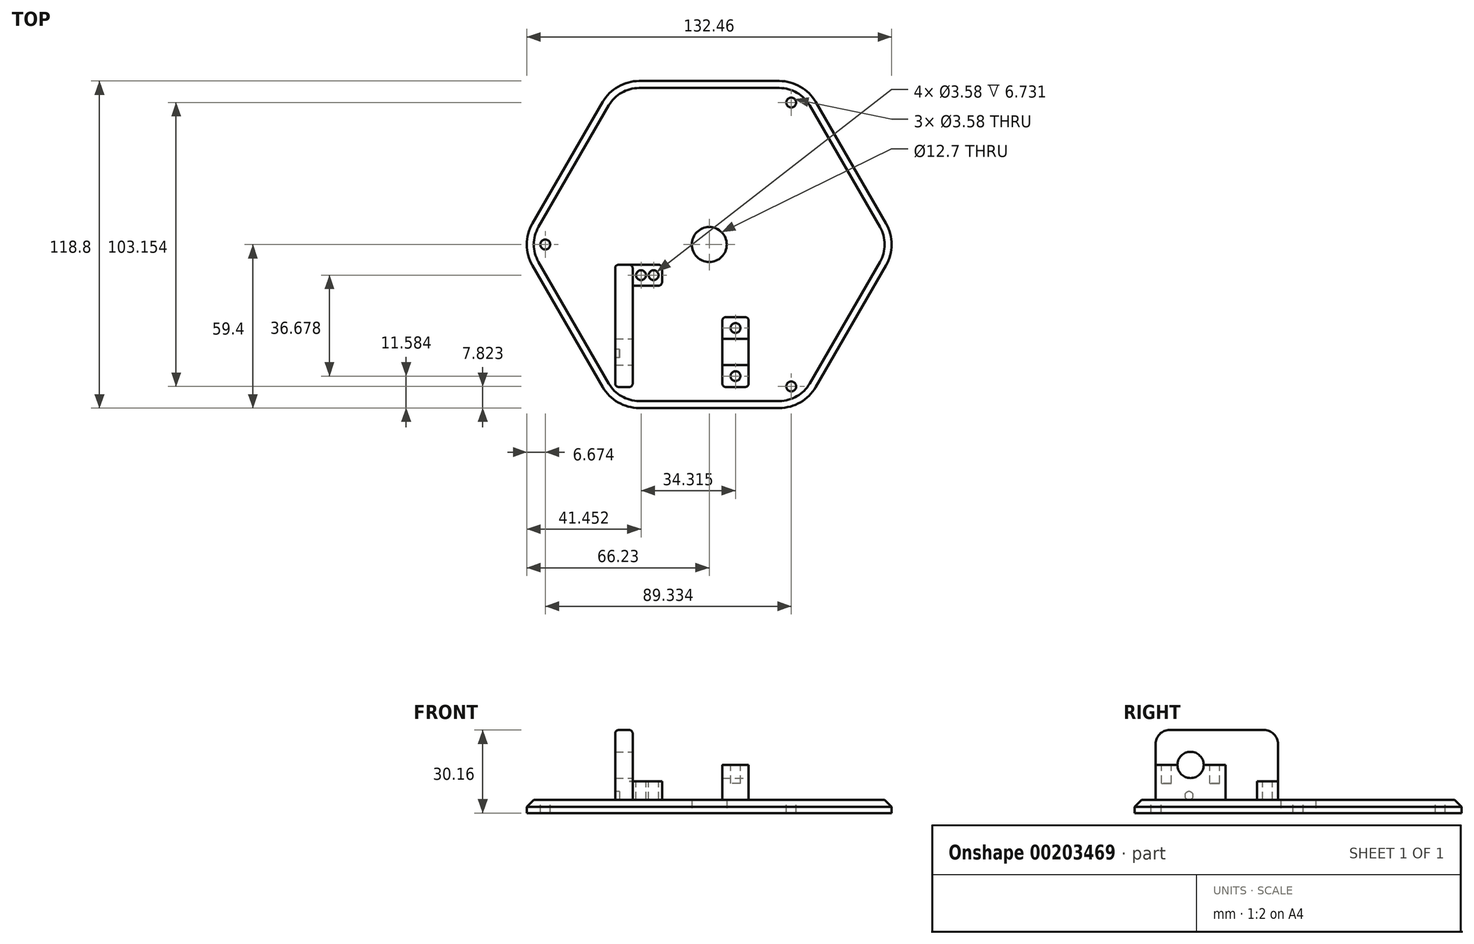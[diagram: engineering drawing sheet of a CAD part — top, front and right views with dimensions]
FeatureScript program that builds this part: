
annotation { "Feature Type Name" : "Feature", "Feature Type Description" : "" }
export const myFeature = defineFeature(function(context is Context, id is Id, definition is map)
    precondition{}
    {
        {
            var Q0;
            Q0=qCreatedBy(makeId("Top.planeOp"),FACE);
            var sketch = newSketch(context, id + "F0", { "sketchPlane" : qUnion([Q0])});
            skCircle(sketch, "E0.cCircle", {"center": v(0, 0) * mm, "radius": 59.4 * mm, "construction": true});
            skLineSegment(sketch, "E0.0", {"start": v(34.3, -59.4) * mm, "end": v(-34.3, -59.4) * mm});
            skLineSegment(sketch, "E0.1", {"start": v(-34.3, -59.4) * mm, "end": v(-68.59, 0) * mm});
            skLineSegment(sketch, "E0.2", {"start": v(-68.59, 0) * mm, "end": v(-34.3, 59.4) * mm});
            skLineSegment(sketch, "E0.3", {"start": v(-34.3, 59.4) * mm, "end": v(34.3, 59.4) * mm});
            skLineSegment(sketch, "E0.4", {"start": v(34.3, 59.4) * mm, "end": v(68.59, 0) * mm});
            skLineSegment(sketch, "E0.5", {"start": v(68.59, 0) * mm, "end": v(34.3, -59.4) * mm});
            skPoint(sketch, "E0.0.midPoint", {"position": v(0, -59.4) * mm});
            skCircle(sketch, "E1", {"center": v(0, 0) * mm, "radius": 6.35 * mm});
            skSolve(sketch);
        }
        {
            var Q0;
            Q0=makeQuery(id+"F0.imprint","IMPRINT",FACE,{"disambiguationData":[TD([[makeQuery(id+"F0.imprint","IMPRINT",EDGE,{"derivedFrom":sQuery(id+"F0.wireOp",EDGE,"E0.0")}),-1.0]])]});
            extrude(context, id + "F1", {"entities" : qUnion([Q0]), "depth" : 4.76 * mm});
        }
        {
            var Q0;
            Q0=makeQuery(id+"F1.opExtrude","CAP_FACE",FACE,{"disambiguationData":[OSD([sQuery(id+"F0.wireOp",EDGE,"E0.0"),sQuery(id+"F0.wireOp",EDGE,"E0.1"),sQuery(id+"F0.wireOp",EDGE,"E0.2"),sQuery(id+"F0.wireOp",EDGE,"E0.3"),sQuery(id+"F0.wireOp",EDGE,"E0.4"),sQuery(id+"F0.wireOp",EDGE,"E0.5"),sQuery(id+"F0.wireOp",EDGE,"E1")])],"isStart":false});
            var sketch = newSketch(context, id + "F2", { "sketchPlane" : qUnion([Q0])});
            skLineSegment(sketch, "E2.bottom", {"start": v(-34.16, -51.78) * mm, "end": v(-27.81, -51.78) * mm});
            skLineSegment(sketch, "E2.top", {"start": v(-34.16, -7.33) * mm, "end": v(-27.81, -7.33) * mm});
            skLineSegment(sketch, "E2.left", {"start": v(-34.16, -51.78) * mm, "end": v(-34.16, -7.33) * mm});
            skLineSegment(sketch, "E2.right", {"start": v(-27.81, -51.78) * mm, "end": v(-27.81, -7.33) * mm});
            skLineSegment(sketch, "E3.bottom", {"start": v(-27.81, -7.33) * mm, "end": v(-17.15, -7.33) * mm});
            skLineSegment(sketch, "E3.top", {"start": v(-27.81, -14.95) * mm, "end": v(-17.15, -14.95) * mm});
            skLineSegment(sketch, "E3.left", {"start": v(-27.81, -7.33) * mm, "end": v(-27.81, -14.95) * mm});
            skLineSegment(sketch, "E3.right", {"start": v(-17.15, -7.33) * mm, "end": v(-17.15, -14.95) * mm});
            skLineSegment(sketch, "E4.bottom", {"start": v(4.78, -51.78) * mm, "end": v(14.3, -51.78) * mm});
            skLineSegment(sketch, "E4.top", {"start": v(4.78, -26.38) * mm, "end": v(14.3, -26.38) * mm});
            skLineSegment(sketch, "E4.left", {"start": v(4.78, -51.78) * mm, "end": v(4.78, -26.38) * mm});
            skLineSegment(sketch, "E4.right", {"start": v(14.3, -51.78) * mm, "end": v(14.3, -26.38) * mm});
            skLineSegment(sketch, "E5.1.0", {"start": v(37.7, 38.27) * mm, "end": v(15.7, 25.57) * mm});
            skLineSegment(sketch, "E5.1.1", {"start": v(42.45, 30.02) * mm, "end": v(20.46, 17.32) * mm});
            skLineSegment(sketch, "E5.1.2", {"start": v(20.46, 17.32) * mm, "end": v(15.7, 25.57) * mm});
            skLineSegment(sketch, "E5.1.3", {"start": v(61.92, -3.7) * mm, "end": v(23.43, -25.92) * mm});
            skLineSegment(sketch, "E5.1.4", {"start": v(58.75, 1.8) * mm, "end": v(20.25, -20.42) * mm});
            skLineSegment(sketch, "E5.1.5", {"start": v(20.25, -20.42) * mm, "end": v(14.92, -11.18) * mm});
            skLineSegment(sketch, "E5.1.6", {"start": v(26.85, -16.61) * mm, "end": v(21.52, -7.37) * mm});
            skLineSegment(sketch, "E5.1.7", {"start": v(42.45, 30.02) * mm, "end": v(37.7, 38.27) * mm});
            skLineSegment(sketch, "E5.1.8", {"start": v(14.92, -11.18) * mm, "end": v(21.52, -7.37) * mm});
            skLineSegment(sketch, "E5.1.9", {"start": v(61.92, -3.7) * mm, "end": v(58.75, 1.8) * mm});
            skLineSegment(sketch, "E5.1.10", {"start": v(23.43, -25.92) * mm, "end": v(20.25, -20.42) * mm});
            skLineSegment(sketch, "E5.1.11", {"start": v(20.25, -20.42) * mm, "end": v(26.85, -16.61) * mm});
            skLineSegment(sketch, "E5.2.0", {"start": v(-52, 13.5) * mm, "end": v(-30, 0.8) * mm});
            skLineSegment(sketch, "E5.2.1", {"start": v(-47.23, 21.75) * mm, "end": v(-25.23, 9.05) * mm});
            skLineSegment(sketch, "E5.2.2", {"start": v(-25.23, 9.05) * mm, "end": v(-30, 0.8) * mm});
            skLineSegment(sketch, "E5.2.3", {"start": v(-27.76, 55.47) * mm, "end": v(10.74, 33.25) * mm});
            skLineSegment(sketch, "E5.2.4", {"start": v(-30.93, 49.98) * mm, "end": v(7.56, 27.75) * mm});
            skLineSegment(sketch, "E5.2.5", {"start": v(7.56, 27.75) * mm, "end": v(2.23, 18.51) * mm});
            skLineSegment(sketch, "E5.2.6", {"start": v(0.96, 31.56) * mm, "end": v(-4.37, 22.32) * mm});
            skLineSegment(sketch, "E5.2.7", {"start": v(-47.23, 21.75) * mm, "end": v(-52, 13.5) * mm});
            skLineSegment(sketch, "E5.2.8", {"start": v(2.23, 18.51) * mm, "end": v(-4.37, 22.32) * mm});
            skLineSegment(sketch, "E5.2.9", {"start": v(-27.76, 55.47) * mm, "end": v(-30.93, 49.98) * mm});
            skLineSegment(sketch, "E5.2.10", {"start": v(10.74, 33.25) * mm, "end": v(7.56, 27.75) * mm});
            skLineSegment(sketch, "E5.2.11", {"start": v(7.56, 27.75) * mm, "end": v(0.96, 31.56) * mm});
            skPoint(sketch, "E5.center", {"position": v(0, 0) * mm});
            skSolve(sketch);
        }
        {
            var Q0;
            Q0=makeQuery(id+"F2.imprint","IMPRINT",FACE,{"disambiguationData":[TD([[makeQuery(id+"F2.imprint","IMPRINT",EDGE,{"derivedFrom":sQuery(id+"F2.wireOp",EDGE,"E2.bottom")}),1.0]])]});
            extrude(context, id + "F3", {"entities" : qUnion([Q0]), "operationType" : NewBodyOperationType.ADD, "depth" : 25.4 * mm});
        }
        {
            var Q0;
            Q0=makeQuery(id+"F2.imprint","IMPRINT",FACE,{"disambiguationData":[TD([[makeQuery(id+"F2.imprint","IMPRINT",EDGE,{"derivedFrom":sQuery(id+"F2.wireOp",EDGE,"E3.bottom")}),-1.0]])]});
            extrude(context, id + "F4", {"entities" : qUnion([Q0]), "operationType" : NewBodyOperationType.ADD, "depth" : 6.73 * mm});
        }
        {
            var Q0;
            Q0=makeQuery(id+"F2.imprint","IMPRINT",FACE,{"disambiguationData":[TD([[makeQuery(id+"F2.imprint","IMPRINT",EDGE,{"derivedFrom":sQuery(id+"F2.wireOp",EDGE,"E4.bottom")}),1.0]])]});
            extrude(context, id + "F5", {"entities" : qUnion([Q0]), "operationType" : NewBodyOperationType.ADD, "depth" : 12.7 * mm});
        }
        {
            var Q0;
            Q0=makeQuery(id+"F5.opExtrude","SWEPT_FACE",FACE,{"disambiguationData":[OSD([sQuery(id+"F2.wireOp",EDGE,"E4.right")])]});
            var sketch = newSketch(context, id + "F6", { "sketchPlane" : qUnion([Q0])});
            skCircle(sketch, "E6", {"center": v(-39.08, 17.46) * mm, "radius": 4.78 * mm});
            skSolve(sketch);
        }
        {
            var Q0;
            {var subQ0=sQuery(id+"F6.wireOp",EDGE,"E6");var subQ1=makeQuery(id+"F5.opExtrude","CAP_EDGE",EDGE,{"disambiguationData":[OSD([sQuery(id+"F2.wireOp",EDGE,"E4.right")])],"isStart":false});var subQ2=makeQuery(id+"F6.imprint","INTERSECT",VERTEX,{"disambiguationData":[OD(0.0)],"derivedFrom":[subQ1,subQ0]});Q0=makeQuery(id+"F6.imprint","IMPRINT",FACE,{"disambiguationData":[TD([[makeQuery(id+"F6.imprint","IMPRINT",EDGE,{"disambiguationData":[TD([[subQ2,-1.0]])],"derivedFrom":subQ0}),1.0]])]});}
            var Q1;
            {var subQ0=sQuery(id+"F6.wireOp",EDGE,"E6");var subQ1=makeQuery(id+"F5.opExtrude","CAP_EDGE",EDGE,{"disambiguationData":[OSD([sQuery(id+"F2.wireOp",EDGE,"E4.right")])],"isStart":false});var subQ2=makeQuery(id+"F6.imprint","INTERSECT",VERTEX,{"disambiguationData":[OD(0.0)],"derivedFrom":[subQ1,subQ0]});Q1=makeQuery(id+"F6.imprint","IMPRINT",FACE,{"disambiguationData":[TD([[makeQuery(id+"F6.imprint","IMPRINT",EDGE,{"disambiguationData":[TD([[subQ2,1.0]])],"derivedFrom":subQ0}),1.0]])]});}
            extrude(context, id + "F7", {"entities" : qUnion([Q0, Q1]), "operationType" : NewBodyOperationType.REMOVE, "oppositeDirection" : true, "depth" : 52.07 * mm});
        }
        {
            var Q0;
            {var subQ0=sQuery(id+"F2.wireOp",EDGE,"E4.top");var subQ1=sQuery(id+"F2.wireOp",EDGE,"E4.left");var subQ2=sQuery(id+"F2.wireOp",EDGE,"E4.right");Q0=makeQuery(id+"F7.boolean.opBoolean","SPLIT",FACE,{"disambiguationData":[TD([makeQuery(id+"F5.opExtrude","SWEPT_FACE",FACE,{"disambiguationData":[OSD([subQ0])]})])],"derivedFrom":makeQuery(id+"F5.opExtrude","CAP_FACE",FACE,{"disambiguationData":[OSD([sQuery(id+"F2.wireOp",EDGE,"E4.bottom"),subQ0,subQ1,subQ2])],"isStart":false})});}
            var sketch = newSketch(context, id + "F8", { "sketchPlane" : qUnion([Q0])});
            skPoint(sketch, "E7", {"position": v(9.54, -30.34) * mm});
            skPoint(sketch, "E7.positionSnap0", {"position": v(9.54, -26.38) * mm});
            skPoint(sketch, "E7.positionSnap1", {"position": v(4.78, -30.34) * mm});
            skCircle(sketch, "E8", {"center": v(9.54, -30.34) * mm, "radius": 1.8 * mm});
            skSolve(sketch);
        }
        {
            var Q0;
            {var subQ0=sQuery(id+"F2.wireOp",EDGE,"E4.bottom");var subQ1=sQuery(id+"F2.wireOp",EDGE,"E4.left");var subQ2=sQuery(id+"F2.wireOp",EDGE,"E4.right");Q0=makeQuery(id+"F7.boolean.opBoolean","SPLIT",FACE,{"disambiguationData":[TD([makeQuery(id+"F5.opExtrude","SWEPT_FACE",FACE,{"disambiguationData":[OSD([subQ0])]})])],"derivedFrom":makeQuery(id+"F5.opExtrude","CAP_FACE",FACE,{"disambiguationData":[OSD([subQ0,sQuery(id+"F2.wireOp",EDGE,"E4.top"),subQ1,subQ2])],"isStart":false})});}
            var sketch = newSketch(context, id + "F9", { "sketchPlane" : qUnion([Q0])});
            skPoint(sketch, "E9", {"position": v(9.54, -47.82) * mm});
            skPoint(sketch, "E9.positionSnap0", {"position": v(9.54, -51.78) * mm});
            skPoint(sketch, "E9.positionSnap1", {"position": v(4.78, -47.82) * mm});
            skCircle(sketch, "E10", {"center": v(9.54, -47.82) * mm, "radius": 1.8 * mm});
            skSolve(sketch);
        }
        {
            var Q0;
            Q0=makeQuery(id+"F8.imprint","IMPRINT",FACE,{"disambiguationData":[TD([[makeQuery(id+"F8.imprint","IMPRINT",EDGE,{"derivedFrom":sQuery(id+"F8.wireOp",EDGE,"E8")}),1.0]])]});
            var Q1;
            Q1=makeQuery(id+"F9.imprint","IMPRINT",FACE,{"disambiguationData":[TD([[makeQuery(id+"F9.imprint","IMPRINT",EDGE,{"derivedFrom":sQuery(id+"F9.wireOp",EDGE,"E10")}),1.0]])]});
            extrude(context, id + "F10", {"entities" : qUnion([Q0, Q1]), "operationType" : NewBodyOperationType.REMOVE, "oppositeDirection" : true, "depth" : 6.73 * mm});
        }
        {
            var Q0;
            Q0=makeQuery(id+"F4.opExtrude","CAP_FACE",FACE,{"disambiguationData":[OSD([sQuery(id+"F2.wireOp",EDGE,"E3.bottom"),sQuery(id+"F2.wireOp",EDGE,"E3.top"),sQuery(id+"F2.wireOp",EDGE,"E3.left"),sQuery(id+"F2.wireOp",EDGE,"E3.right")])],"isStart":false});
            var sketch = newSketch(context, id + "F11", { "sketchPlane" : qUnion([Q0])});
            skCircle(sketch, "E11", {"center": v(-24.78, -11.14) * mm, "radius": 1.8 * mm});
            skPoint(sketch, "E11.centerSnap0", {"position": v(-27.81, -11.14) * mm});
            skCircle(sketch, "E12", {"center": v(-20.2, -11.14) * mm, "radius": 1.8 * mm});
            skSolve(sketch);
        }
        {
            var Q0;
            Q0=makeQuery(id+"F11.imprint","IMPRINT",FACE,{"disambiguationData":[TD([[makeQuery(id+"F11.imprint","IMPRINT",EDGE,{"derivedFrom":sQuery(id+"F11.wireOp",EDGE,"E11")}),1.0]])]});
            var Q1;
            Q1=makeQuery(id+"F11.imprint","IMPRINT",FACE,{"disambiguationData":[TD([[makeQuery(id+"F11.imprint","IMPRINT",EDGE,{"derivedFrom":sQuery(id+"F11.wireOp",EDGE,"E12")}),1.0]])]});
            extrude(context, id + "F12", {"entities" : qUnion([Q0, Q1]), "operationType" : NewBodyOperationType.REMOVE, "oppositeDirection" : true, "depth" : 6.73 * mm});
        }
        {
            var Q0;
            Q0=makeQuery(id+"F3.opExtrude","CAP_EDGE",EDGE,{"disambiguationData":[OSD([sQuery(id+"F2.wireOp",EDGE,"E2.top")])],"isStart":false});
            var Q1;
            Q1=makeQuery(id+"F3.opExtrude","CAP_EDGE",EDGE,{"disambiguationData":[OSD([sQuery(id+"F2.wireOp",EDGE,"E2.bottom")])],"isStart":false});
            fillet(context, id + "F13", {"entities" : qUnion([Q0, Q1]), "radius" : 5.08 * mm, "tangentPropagation" : true, "allowEdgeOverflow" : false});
        }
        {
            var Q0;
            Q0=makeQuery(id+"F3.opExtrude","CAP_EDGE",EDGE,{"disambiguationData":[OSD([sQuery(id+"F2.wireOp",EDGE,"E2.left")])],"isStart":true});
            var Q1;
            Q1=makeQuery(id+"F3.opExtrude","CAP_EDGE",EDGE,{"disambiguationData":[OSD([sQuery(id+"F2.wireOp",EDGE,"E2.bottom")])],"isStart":true});
            var Q2;
            Q2=makeQuery(id+"F3.opExtrude","SWEPT_EDGE",EDGE,{"disambiguationData":[OSD([sQuery(id+"F2.wireOp",EDGE,"E2.bottom"),sQuery(id+"F2.wireOp",EDGE,"E2.left")])]});
            var Q3;
            Q3=makeQuery(id+"F3.opExtrude","SWEPT_EDGE",EDGE,{"disambiguationData":[OSD([sQuery(id+"F2.wireOp",EDGE,"E2.bottom"),sQuery(id+"F2.wireOp",EDGE,"E2.right")])]});
            var Q4;
            Q4=makeQuery(id+"F4.opExtrude","CAP_EDGE",EDGE,{"disambiguationData":[OSD([sQuery(id+"F2.wireOp",EDGE,"E3.top")])],"isStart":true});
            var Q5;
            Q5=makeQuery(id+"F4.opExtrude","CAP_EDGE",EDGE,{"disambiguationData":[OSD([sQuery(id+"F2.wireOp",EDGE,"E3.right")])],"isStart":true});
            var Q6;
            Q6=makeQuery(id+"F4.opExtrude","SWEPT_EDGE",EDGE,{"disambiguationData":[OSD([sQuery(id+"F2.wireOp",EDGE,"E3.bottom"),sQuery(id+"F2.wireOp",EDGE,"E3.right")])]});
            var Q7;
            Q7=makeQuery(id+"F4.opExtrude","SWEPT_EDGE",EDGE,{"disambiguationData":[OSD([sQuery(id+"F2.wireOp",EDGE,"E3.top"),sQuery(id+"F2.wireOp",EDGE,"E3.right")])]});
            var Q8;
            Q8=makeQuery(id+"F5.opExtrude","SWEPT_EDGE",EDGE,{"disambiguationData":[OSD([sQuery(id+"F2.wireOp",EDGE,"E4.bottom"),sQuery(id+"F2.wireOp",EDGE,"E4.left")])]});
            var Q9;
            Q9=makeQuery(id+"F5.opExtrude","SWEPT_EDGE",EDGE,{"disambiguationData":[OSD([sQuery(id+"F2.wireOp",EDGE,"E4.bottom"),sQuery(id+"F2.wireOp",EDGE,"E4.right")])]});
            var Q10;
            Q10=makeQuery(id+"F5.opExtrude","SWEPT_EDGE",EDGE,{"disambiguationData":[OSD([sQuery(id+"F2.wireOp",EDGE,"E4.top"),sQuery(id+"F2.wireOp",EDGE,"E4.right")])]});
            var Q11;
            Q11=makeQuery(id+"F5.opExtrude","SWEPT_EDGE",EDGE,{"disambiguationData":[OSD([sQuery(id+"F2.wireOp",EDGE,"E4.top"),sQuery(id+"F2.wireOp",EDGE,"E4.left")])]});
            fillet(context, id + "F14", {"entities" : qUnion([Q0, Q1, Q2, Q3, Q4, Q5, Q6, Q7, Q8, Q9, Q10, Q11]), "radius" : 1.27 * mm, "tangentPropagation" : true, "allowEdgeOverflow" : false});
        }
        {
            var Q0;
            Q0=makeQuery(id+"F3.opExtrude","SWEPT_FACE",FACE,{"disambiguationData":[OSD([sQuery(id+"F2.wireOp",EDGE,"E2.left")])]});
            var sketch = newSketch(context, id + "F15", { "sketchPlane" : qUnion([Q0])});
            skCircle(sketch, "E13", {"center": v(39.64, 6.29) * mm, "radius": 1.52 * mm});
            skSolve(sketch);
        }
        {
            var Q0;
            {var subQ0=sQuery(id+"F15.wireOp",EDGE,"E13");var subQ1=sQuery(id+"F2.wireOp",EDGE,"E2.left");var subQ2=makeQuery(id+"F14.opFillet","BLEND_EDGE",EDGE,{"blendedFrom":[makeQuery(id+"F3.opExtrude","CAP_EDGE",EDGE,{"disambiguationData":[OSD([subQ1])],"isStart":true}),makeQuery(id+"F3.opExtrude","SWEPT_FACE",FACE,{"disambiguationData":[OSD([subQ1])]})],"blendedInto":[makeQuery(id+"F3.opExtrude","SWEPT_FACE",FACE,{"disambiguationData":[OSD([subQ1])]})]});var subQ3=makeQuery(id+"F15.imprint","INTERSECT",VERTEX,{"disambiguationData":[OD(0.0)],"derivedFrom":[subQ2,subQ0]});Q0=makeQuery(id+"F15.imprint","IMPRINT",FACE,{"disambiguationData":[TD([[makeQuery(id+"F15.imprint","IMPRINT",EDGE,{"disambiguationData":[TD([[subQ3,1.0]])],"derivedFrom":subQ0}),1.0]])]});}
            var Q1;
            {var subQ0=sQuery(id+"F15.wireOp",EDGE,"E13");var subQ1=sQuery(id+"F2.wireOp",EDGE,"E2.left");var subQ2=makeQuery(id+"F14.opFillet","BLEND_EDGE",EDGE,{"blendedFrom":[makeQuery(id+"F3.opExtrude","CAP_EDGE",EDGE,{"disambiguationData":[OSD([subQ1])],"isStart":true}),makeQuery(id+"F3.opExtrude","SWEPT_FACE",FACE,{"disambiguationData":[OSD([subQ1])]})],"blendedInto":[makeQuery(id+"F3.opExtrude","SWEPT_FACE",FACE,{"disambiguationData":[OSD([subQ1])]})]});var subQ3=makeQuery(id+"F15.imprint","INTERSECT",VERTEX,{"disambiguationData":[OD(0.0)],"derivedFrom":[subQ2,subQ0]});Q1=makeQuery(id+"F15.imprint","IMPRINT",FACE,{"disambiguationData":[TD([[makeQuery(id+"F15.imprint","IMPRINT",EDGE,{"disambiguationData":[TD([[subQ3,-1.0]])],"derivedFrom":subQ0}),1.0]])]});}
            extrude(context, id + "F16", {"entities" : qUnion([Q0, Q1]), "operationType" : NewBodyOperationType.REMOVE, "endBound" : BoundingType.SYMMETRIC, "oppositeDirection" : true, "depth" : 3.17 * mm});
        }
        {
            var Q0;
            Q0=makeQuery(id+"F1.opExtrude","SWEPT_EDGE",EDGE,{"disambiguationData":[OSD([sQuery(id+"F0.wireOp",EDGE,"E0.2"),sQuery(id+"F0.wireOp",EDGE,"E0.3")])]});
            var Q1;
            Q1=makeQuery(id+"F1.opExtrude","SWEPT_EDGE",EDGE,{"disambiguationData":[OSD([sQuery(id+"F0.wireOp",EDGE,"E0.1"),sQuery(id+"F0.wireOp",EDGE,"E0.2")])]});
            var Q2;
            Q2=makeQuery(id+"F1.opExtrude","SWEPT_EDGE",EDGE,{"disambiguationData":[OSD([sQuery(id+"F0.wireOp",EDGE,"E0.3"),sQuery(id+"F0.wireOp",EDGE,"E0.4")])]});
            var Q3;
            Q3=makeQuery(id+"F1.opExtrude","SWEPT_EDGE",EDGE,{"disambiguationData":[OSD([sQuery(id+"F0.wireOp",EDGE,"E0.0"),sQuery(id+"F0.wireOp",EDGE,"E0.1")])]});
            var Q4;
            Q4=makeQuery(id+"F1.opExtrude","SWEPT_EDGE",EDGE,{"disambiguationData":[OSD([sQuery(id+"F0.wireOp",EDGE,"E0.0"),sQuery(id+"F0.wireOp",EDGE,"E0.5")])]});
            var Q5;
            Q5=makeQuery(id+"F1.opExtrude","SWEPT_EDGE",EDGE,{"disambiguationData":[OSD([sQuery(id+"F0.wireOp",EDGE,"E0.4"),sQuery(id+"F0.wireOp",EDGE,"E0.5")])]});
            fillet(context, id + "F17", {"entities" : qUnion([Q0, Q1, Q2, Q3, Q4, Q5]), "radius" : 15.24 * mm, "tangentPropagation" : true, "allowEdgeOverflow" : false});
        }
        {
            var Q0;
            Q0=makeQuery(id+"F1.opExtrude","CAP_EDGE",EDGE,{"disambiguationData":[OSD([sQuery(id+"F0.wireOp",EDGE,"E0.2")])],"isStart":false});
            var Q1;
            Q1=makeQuery(id+"F1.opExtrude","CAP_EDGE",EDGE,{"disambiguationData":[OSD([sQuery(id+"F0.wireOp",EDGE,"E0.1")])],"isStart":false});
            var Q2;
            {var subQ0=sQuery(id+"F0.wireOp",EDGE,"E0.2");var subQ1=sQuery(id+"F0.wireOp",EDGE,"E0.1");Q2=makeQuery(id+"F17.opFillet","BLEND_EDGE",EDGE,{"blendedFrom":[makeQuery(id+"F1.opExtrude","SWEPT_EDGE",EDGE,{"disambiguationData":[OSD([subQ1,subQ0])]}),makeQuery(id+"F1.opExtrude","CAP_FACE",FACE,{"disambiguationData":[OSD([sQuery(id+"F0.wireOp",EDGE,"E0.0"),subQ1,subQ0,sQuery(id+"F0.wireOp",EDGE,"E0.3"),sQuery(id+"F0.wireOp",EDGE,"E0.4"),sQuery(id+"F0.wireOp",EDGE,"E0.5"),sQuery(id+"F0.wireOp",EDGE,"E1")])],"isStart":false})],"blendedInto":[makeQuery(id+"F1.opExtrude","CAP_FACE",FACE,{"disambiguationData":[OSD([sQuery(id+"F0.wireOp",EDGE,"E0.0"),subQ1,subQ0,sQuery(id+"F0.wireOp",EDGE,"E0.3"),sQuery(id+"F0.wireOp",EDGE,"E0.4"),sQuery(id+"F0.wireOp",EDGE,"E0.5"),sQuery(id+"F0.wireOp",EDGE,"E1")])],"isStart":false})]});}
            var Q3;
            {var subQ0=sQuery(id+"F0.wireOp",EDGE,"E0.1");var subQ1=sQuery(id+"F0.wireOp",EDGE,"E0.0");Q3=makeQuery(id+"F17.opFillet","BLEND_EDGE",EDGE,{"blendedFrom":[makeQuery(id+"F1.opExtrude","SWEPT_EDGE",EDGE,{"disambiguationData":[OSD([subQ1,subQ0])]}),makeQuery(id+"F1.opExtrude","CAP_FACE",FACE,{"disambiguationData":[OSD([subQ1,subQ0,sQuery(id+"F0.wireOp",EDGE,"E0.2"),sQuery(id+"F0.wireOp",EDGE,"E0.3"),sQuery(id+"F0.wireOp",EDGE,"E0.4"),sQuery(id+"F0.wireOp",EDGE,"E0.5"),sQuery(id+"F0.wireOp",EDGE,"E1")])],"isStart":false})],"blendedInto":[makeQuery(id+"F1.opExtrude","CAP_FACE",FACE,{"disambiguationData":[OSD([subQ1,subQ0,sQuery(id+"F0.wireOp",EDGE,"E0.2"),sQuery(id+"F0.wireOp",EDGE,"E0.3"),sQuery(id+"F0.wireOp",EDGE,"E0.4"),sQuery(id+"F0.wireOp",EDGE,"E0.5"),sQuery(id+"F0.wireOp",EDGE,"E1")])],"isStart":false})]});}
            var Q4;
            Q4=makeQuery(id+"F1.opExtrude","CAP_EDGE",EDGE,{"disambiguationData":[OSD([sQuery(id+"F0.wireOp",EDGE,"E0.0")])],"isStart":false});
            var Q5;
            {var subQ0=sQuery(id+"F0.wireOp",EDGE,"E0.5");var subQ1=sQuery(id+"F0.wireOp",EDGE,"E0.0");Q5=makeQuery(id+"F17.opFillet","BLEND_EDGE",EDGE,{"blendedFrom":[makeQuery(id+"F1.opExtrude","SWEPT_EDGE",EDGE,{"disambiguationData":[OSD([subQ1,subQ0])]}),makeQuery(id+"F1.opExtrude","CAP_FACE",FACE,{"disambiguationData":[OSD([subQ1,sQuery(id+"F0.wireOp",EDGE,"E0.1"),sQuery(id+"F0.wireOp",EDGE,"E0.2"),sQuery(id+"F0.wireOp",EDGE,"E0.3"),sQuery(id+"F0.wireOp",EDGE,"E0.4"),subQ0,sQuery(id+"F0.wireOp",EDGE,"E1")])],"isStart":false})],"blendedInto":[makeQuery(id+"F1.opExtrude","CAP_FACE",FACE,{"disambiguationData":[OSD([subQ1,sQuery(id+"F0.wireOp",EDGE,"E0.1"),sQuery(id+"F0.wireOp",EDGE,"E0.2"),sQuery(id+"F0.wireOp",EDGE,"E0.3"),sQuery(id+"F0.wireOp",EDGE,"E0.4"),subQ0,sQuery(id+"F0.wireOp",EDGE,"E1")])],"isStart":false})]});}
            var Q6;
            Q6=makeQuery(id+"F1.opExtrude","CAP_EDGE",EDGE,{"disambiguationData":[OSD([sQuery(id+"F0.wireOp",EDGE,"E0.5")])],"isStart":false});
            var Q7;
            {var subQ0=sQuery(id+"F0.wireOp",EDGE,"E0.5");var subQ1=sQuery(id+"F0.wireOp",EDGE,"E0.4");Q7=makeQuery(id+"F17.opFillet","BLEND_EDGE",EDGE,{"blendedFrom":[makeQuery(id+"F1.opExtrude","SWEPT_EDGE",EDGE,{"disambiguationData":[OSD([subQ1,subQ0])]}),makeQuery(id+"F1.opExtrude","CAP_FACE",FACE,{"disambiguationData":[OSD([sQuery(id+"F0.wireOp",EDGE,"E0.0"),sQuery(id+"F0.wireOp",EDGE,"E0.1"),sQuery(id+"F0.wireOp",EDGE,"E0.2"),sQuery(id+"F0.wireOp",EDGE,"E0.3"),subQ1,subQ0,sQuery(id+"F0.wireOp",EDGE,"E1")])],"isStart":false})],"blendedInto":[makeQuery(id+"F1.opExtrude","CAP_FACE",FACE,{"disambiguationData":[OSD([sQuery(id+"F0.wireOp",EDGE,"E0.0"),sQuery(id+"F0.wireOp",EDGE,"E0.1"),sQuery(id+"F0.wireOp",EDGE,"E0.2"),sQuery(id+"F0.wireOp",EDGE,"E0.3"),subQ1,subQ0,sQuery(id+"F0.wireOp",EDGE,"E1")])],"isStart":false})]});}
            var Q8;
            Q8=makeQuery(id+"F1.opExtrude","CAP_EDGE",EDGE,{"disambiguationData":[OSD([sQuery(id+"F0.wireOp",EDGE,"E0.4")])],"isStart":false});
            var Q9;
            {var subQ0=sQuery(id+"F0.wireOp",EDGE,"E0.4");var subQ1=sQuery(id+"F0.wireOp",EDGE,"E0.3");Q9=makeQuery(id+"F17.opFillet","BLEND_EDGE",EDGE,{"blendedFrom":[makeQuery(id+"F1.opExtrude","SWEPT_EDGE",EDGE,{"disambiguationData":[OSD([subQ1,subQ0])]}),makeQuery(id+"F1.opExtrude","CAP_FACE",FACE,{"disambiguationData":[OSD([sQuery(id+"F0.wireOp",EDGE,"E0.0"),sQuery(id+"F0.wireOp",EDGE,"E0.1"),sQuery(id+"F0.wireOp",EDGE,"E0.2"),subQ1,subQ0,sQuery(id+"F0.wireOp",EDGE,"E0.5"),sQuery(id+"F0.wireOp",EDGE,"E1")])],"isStart":false})],"blendedInto":[makeQuery(id+"F1.opExtrude","CAP_FACE",FACE,{"disambiguationData":[OSD([sQuery(id+"F0.wireOp",EDGE,"E0.0"),sQuery(id+"F0.wireOp",EDGE,"E0.1"),sQuery(id+"F0.wireOp",EDGE,"E0.2"),subQ1,subQ0,sQuery(id+"F0.wireOp",EDGE,"E0.5"),sQuery(id+"F0.wireOp",EDGE,"E1")])],"isStart":false})]});}
            var Q10;
            Q10=makeQuery(id+"F1.opExtrude","CAP_EDGE",EDGE,{"disambiguationData":[OSD([sQuery(id+"F0.wireOp",EDGE,"E0.3")])],"isStart":false});
            var Q11;
            {var subQ0=sQuery(id+"F0.wireOp",EDGE,"E0.3");var subQ1=sQuery(id+"F0.wireOp",EDGE,"E0.2");Q11=makeQuery(id+"F17.opFillet","BLEND_EDGE",EDGE,{"blendedFrom":[makeQuery(id+"F1.opExtrude","SWEPT_EDGE",EDGE,{"disambiguationData":[OSD([subQ1,subQ0])]}),makeQuery(id+"F1.opExtrude","CAP_FACE",FACE,{"disambiguationData":[OSD([sQuery(id+"F0.wireOp",EDGE,"E0.0"),sQuery(id+"F0.wireOp",EDGE,"E0.1"),subQ1,subQ0,sQuery(id+"F0.wireOp",EDGE,"E0.4"),sQuery(id+"F0.wireOp",EDGE,"E0.5"),sQuery(id+"F0.wireOp",EDGE,"E1")])],"isStart":false})],"blendedInto":[makeQuery(id+"F1.opExtrude","CAP_FACE",FACE,{"disambiguationData":[OSD([sQuery(id+"F0.wireOp",EDGE,"E0.0"),sQuery(id+"F0.wireOp",EDGE,"E0.1"),subQ1,subQ0,sQuery(id+"F0.wireOp",EDGE,"E0.4"),sQuery(id+"F0.wireOp",EDGE,"E0.5"),sQuery(id+"F0.wireOp",EDGE,"E1")])],"isStart":false})]});}
            chamfer(context, id + "F18", {"entities" : qUnion([Q0, Q1, Q2, Q3, Q4, Q5, Q6, Q7, Q8, Q9, Q10, Q11]), "width" : 2.54 * mm, "tangentPropagation" : true});
        }
        {
            var Q0;
            Q0=makeQuery(id+"F2.imprint","IMPRINT",FACE,{"disambiguationData":[TD([[makeQuery(id+"F2.imprint","IMPRINT",EDGE,{"derivedFrom":sQuery(id+"F2.wireOp",EDGE,"E2.bottom")}),-1.0]])]});
            var sketch = newSketch(context, id + "F19", { "sketchPlane" : qUnion([Q0])});
            skPoint(sketch, "E14", {"position": v(-59.56, 0) * mm});
            skPoint(sketch, "E15.1.0", {"position": v(29.78, -51.58) * mm});
            skPoint(sketch, "E15.2.0", {"position": v(29.78, 51.58) * mm});
            skPoint(sketch, "E15.center", {"position": v(0, 0) * mm});
            skSolve(sketch);
        }
        {
            var Q0;
            Q0=sQuery(id+"F19.wireOp",VERTEX,"E14");
            var Q1;
            Q1=sQuery(id+"F19.wireOp",VERTEX,"E15.2.0");
            var Q2;
            Q2=sQuery(id+"F19.wireOp",VERTEX,"E15.1.0");
            var Q3;
            Q3=makeQuery(id+"F1.opExtrude","SWEPT_BODY",BODY,{"disambiguationData":[OSD([sQuery(id+"F0.wireOp",EDGE,"E0.0"),sQuery(id+"F0.wireOp",EDGE,"E0.1"),sQuery(id+"F0.wireOp",EDGE,"E0.2"),sQuery(id+"F0.wireOp",EDGE,"E0.3"),sQuery(id+"F0.wireOp",EDGE,"E0.4"),sQuery(id+"F0.wireOp",EDGE,"E0.5"),sQuery(id+"F0.wireOp",EDGE,"E1")])]});
            hole(context, id + "F20", {"style" : HoleStyle.SIMPLE, "endStyle" : HoleEndStyle.BLIND, "holeDiameter" : 3.58 * mm, "holeDepth" : 4.76 * mm, "locations" : qUnion([Q0, Q1, Q2]), "scope" : qUnion([Q3])});
        }
    });
